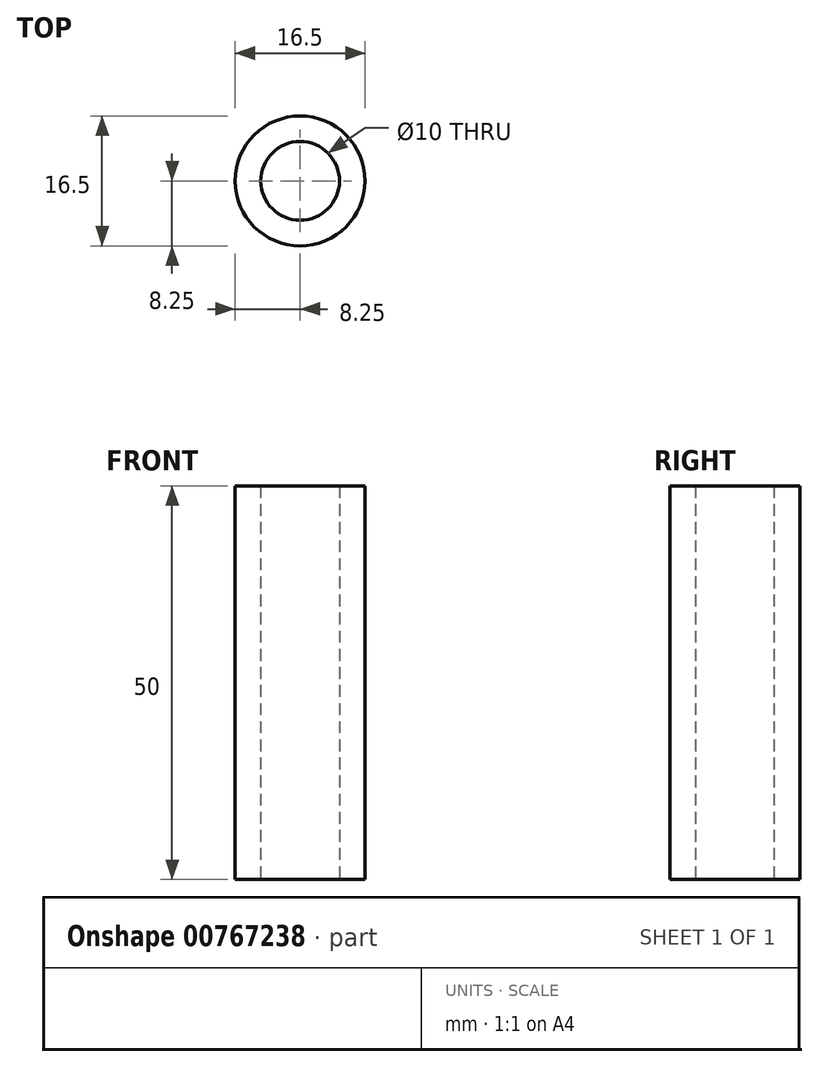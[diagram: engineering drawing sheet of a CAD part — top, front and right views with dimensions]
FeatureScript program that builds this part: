
annotation { "Feature Type Name" : "Feature", "Feature Type Description" : "" }
export const myFeature = defineFeature(function(context is Context, id is Id, definition is map)
    precondition{}
    {
        {
            var Q0;
            Q0=qCreatedBy(makeId("Top.planeOp"),FACE);
            var sketch = newSketch(context, id + "F0", { "sketchPlane" : qUnion([Q0])});
            skCircle(sketch, "E0", {"center": v(0, 0) * mm, "radius": 5 * mm});
            skCircle(sketch, "E1", {"center": v(0, 0) * mm, "radius": 8.25 * mm});
            skSolve(sketch);
        }
        {
            var Q0;
            Q0=makeQuery(id+"F0.imprint","IMPRINT",FACE,{"disambiguationData":[TD([[makeQuery(id+"F0.imprint","IMPRINT",EDGE,{"derivedFrom":sQuery(id+"F0.wireOp",EDGE,"E0")}),-1.0]])]});
            extrude(context, id + "F1", {"entities" : qUnion([Q0]), "depth" : 50 * mm, "offsetDistance" : 25 * mm});
        }
    });
